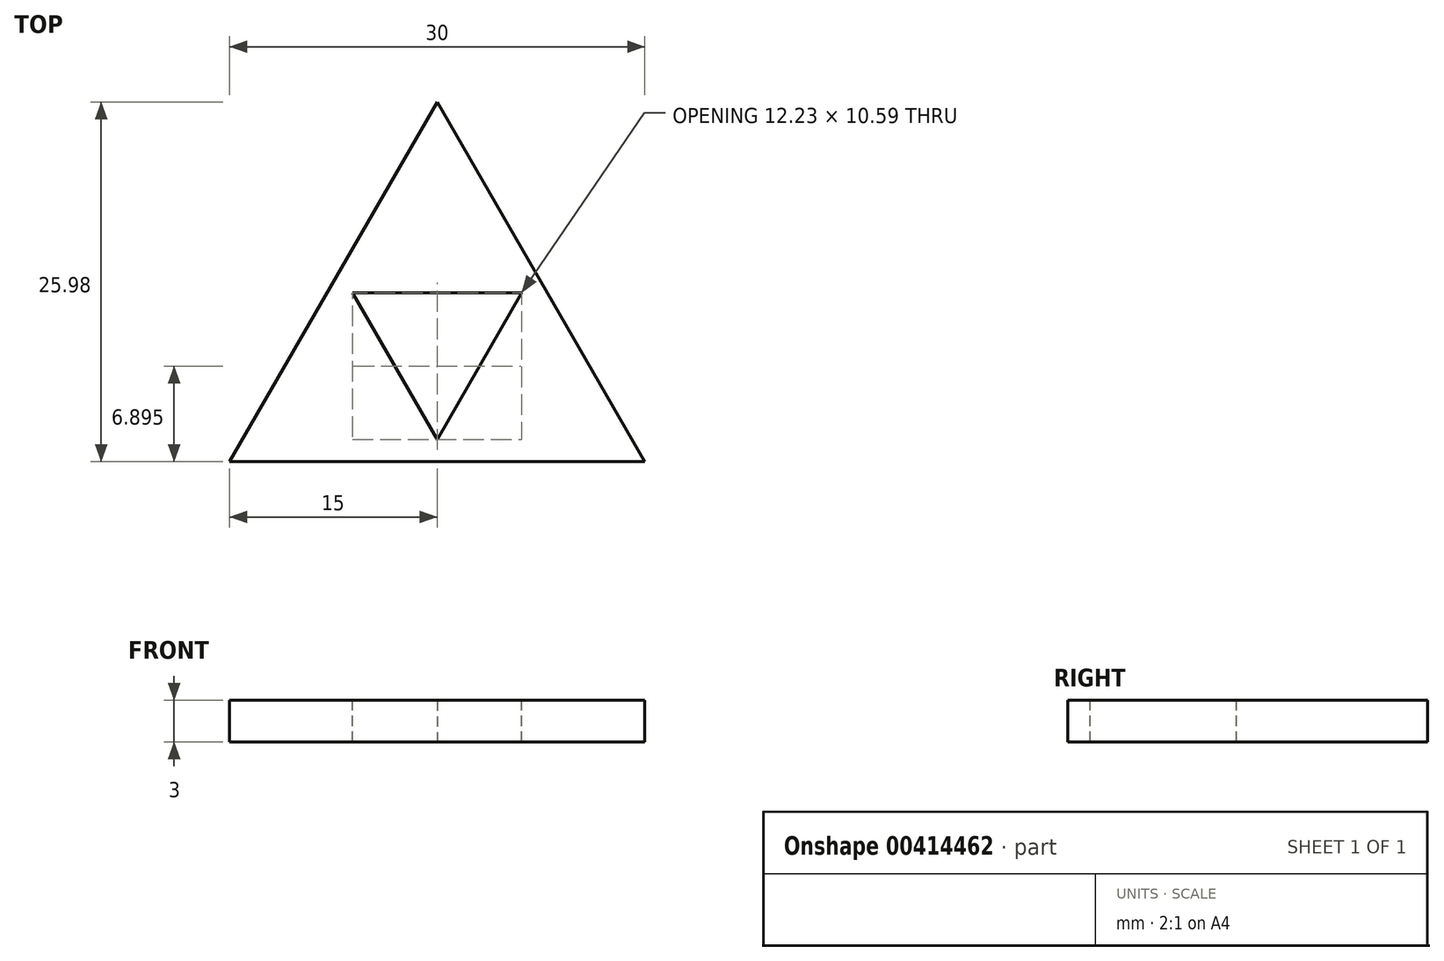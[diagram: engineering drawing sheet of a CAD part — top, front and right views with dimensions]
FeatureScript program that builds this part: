
annotation { "Feature Type Name" : "Feature", "Feature Type Description" : "" }
export const myFeature = defineFeature(function(context is Context, id is Id, definition is map)
    precondition{}
    {
        {
            var Q0;
            Q0=qCreatedBy(makeId("Top.planeOp"),FACE);
            var sketch = newSketch(context, id + "F0", { "sketchPlane" : qUnion([Q0])});
            skCircle(sketch, "E0.cCircle", {"center": v(0, 0) * mm, "radius": 17.32 * mm, "construction": true});
            skLineSegment(sketch, "E0.0", {"start": v(15, -8.66) * mm, "end": v(-15, -8.66) * mm});
            skLineSegment(sketch, "E0.1", {"start": v(-15, -8.66) * mm, "end": v(0, 17.32) * mm});
            skLineSegment(sketch, "E0.2", {"start": v(0, 17.32) * mm, "end": v(15, -8.66) * mm});
            skLineSegment(sketch, "E1", {"start": v(-17.32, 0) * mm, "end": v(17.32, 0) * mm, "construction": true});
            skSolve(sketch);
        }
        {
            var Q0;
            Q0=makeQuery(id+"F0.imprint","IMPRINT",FACE,{"disambiguationData":[TD([[makeQuery(id+"F0.imprint","IMPRINT",EDGE,{"derivedFrom":sQuery(id+"F0.wireOp",EDGE,"E0.0")}),-1.0]])]});
            extrude(context, id + "F1", {"entities" : qUnion([Q0]), "depth" : 1.5 * mm});
        }
        {
            var Q0;
            Q0=makeQuery(id+"F1.opExtrude","CAP_FACE",FACE,{"disambiguationData":[OSD([sQuery(id+"F0.wireOp",EDGE,"E0.0"),sQuery(id+"F0.wireOp",EDGE,"E0.1"),sQuery(id+"F0.wireOp",EDGE,"E0.2")])],"isStart":false});
            var sketch = newSketch(context, id + "F2", { "sketchPlane" : qUnion([Q0])});
            skPoint(sketch, "E2", {"position": v(-7.5, 4.33) * mm});
            skPoint(sketch, "E3", {"position": v(7.5, 4.33) * mm});
            skPoint(sketch, "E4", {"position": v(0, -8.66) * mm});
            skLineSegment(sketch, "E5", {"start": v(-7.5, 4.33) * mm, "end": v(0, -8.66) * mm});
            skLineSegment(sketch, "E6", {"start": v(0, -8.66) * mm, "end": v(7.5, 4.33) * mm});
            skLineSegment(sketch, "E7", {"start": v(7.5, 4.33) * mm, "end": v(-7.5, 4.33) * mm});
            skSolve(sketch);
        }
        {
            var Q0;
            Q0=makeQuery(id+"F2.imprint","IMPRINT",FACE,{"disambiguationData":[TD([[makeQuery(id+"F2.imprint","IMPRINT",EDGE,{"derivedFrom":sQuery(id+"F2.wireOp",EDGE,"E5")}),1.0]])]});
            var sketch = newSketch(context, id + "F3", { "sketchPlane" : qUnion([Q0])});
            skLineSegment(sketch, "E8.0", {"start": v(-7.5, 4.33) * mm, "end": v(0, -8.66) * mm, "construction": true});
            skLineSegment(sketch, "E9.0", {"start": v(7.5, 4.33) * mm, "end": v(-7.5, 4.33) * mm, "construction": true});
            skLineSegment(sketch, "E10.0", {"start": v(0, -8.66) * mm, "end": v(7.5, 4.33) * mm, "construction": true});
            skLineSegment(sketch, "E11.0", {"start": v(6.11, 3.53) * mm, "end": v(-6.11, 3.53) * mm});
            skLineSegment(sketch, "E11.1", {"start": v(0, -7.06) * mm, "end": v(6.11, 3.53) * mm});
            skLineSegment(sketch, "E11.2", {"start": v(-6.11, 3.53) * mm, "end": v(0, -7.06) * mm});
            skSolve(sketch);
        }
        {
            var Q0;
            Q0=makeQuery(id+"F3.imprint","IMPRINT",FACE,{"disambiguationData":[TD([[makeQuery(id+"F3.imprint","IMPRINT",EDGE,{"derivedFrom":sQuery(id+"F3.wireOp",EDGE,"E11.0")}),1.0]])]});
            extrude(context, id + "F4", {"entities" : qUnion([Q0]), "operationType" : NewBodyOperationType.REMOVE, "oppositeDirection" : true, "depth" : 1.5 * mm});
        }
        {
            var Q0;
            Q0=makeQuery(id+"F1.opExtrude","CAP_FACE",FACE,{"disambiguationData":[OSD([sQuery(id+"F0.wireOp",EDGE,"E0.0"),sQuery(id+"F0.wireOp",EDGE,"E0.1"),sQuery(id+"F0.wireOp",EDGE,"E0.2")])],"isStart":false});
            extrude(context, id + "F5", {"entities" : qUnion([Q0]), "operationType" : NewBodyOperationType.ADD, "depth" : 1.5 * mm});
        }
        {
            var Q0;
            Q0=makeQuery(id+"F1.opExtrude","CAP_FACE",FACE,{"disambiguationData":[OSD([sQuery(id+"F0.wireOp",EDGE,"E0.0"),sQuery(id+"F0.wireOp",EDGE,"E0.1"),sQuery(id+"F0.wireOp",EDGE,"E0.2")])],"isStart":true});
            var sketch = newSketch(context, id + "F6", { "sketchPlane" : qUnion([Q0])});
            skLineSegment(sketch, "E12.0.0", {"start": v(0, -17.32) * mm, "end": v(15, 8.66) * mm, "construction": true});
            skLineSegment(sketch, "E12.0.1", {"start": v(15, 8.66) * mm, "end": v(-15, 8.66) * mm, "construction": true});
            skLineSegment(sketch, "E12.0.2", {"start": v(-15, 8.66) * mm, "end": v(0, -17.32) * mm, "construction": true});
            skSolve(sketch);
        }
    });
